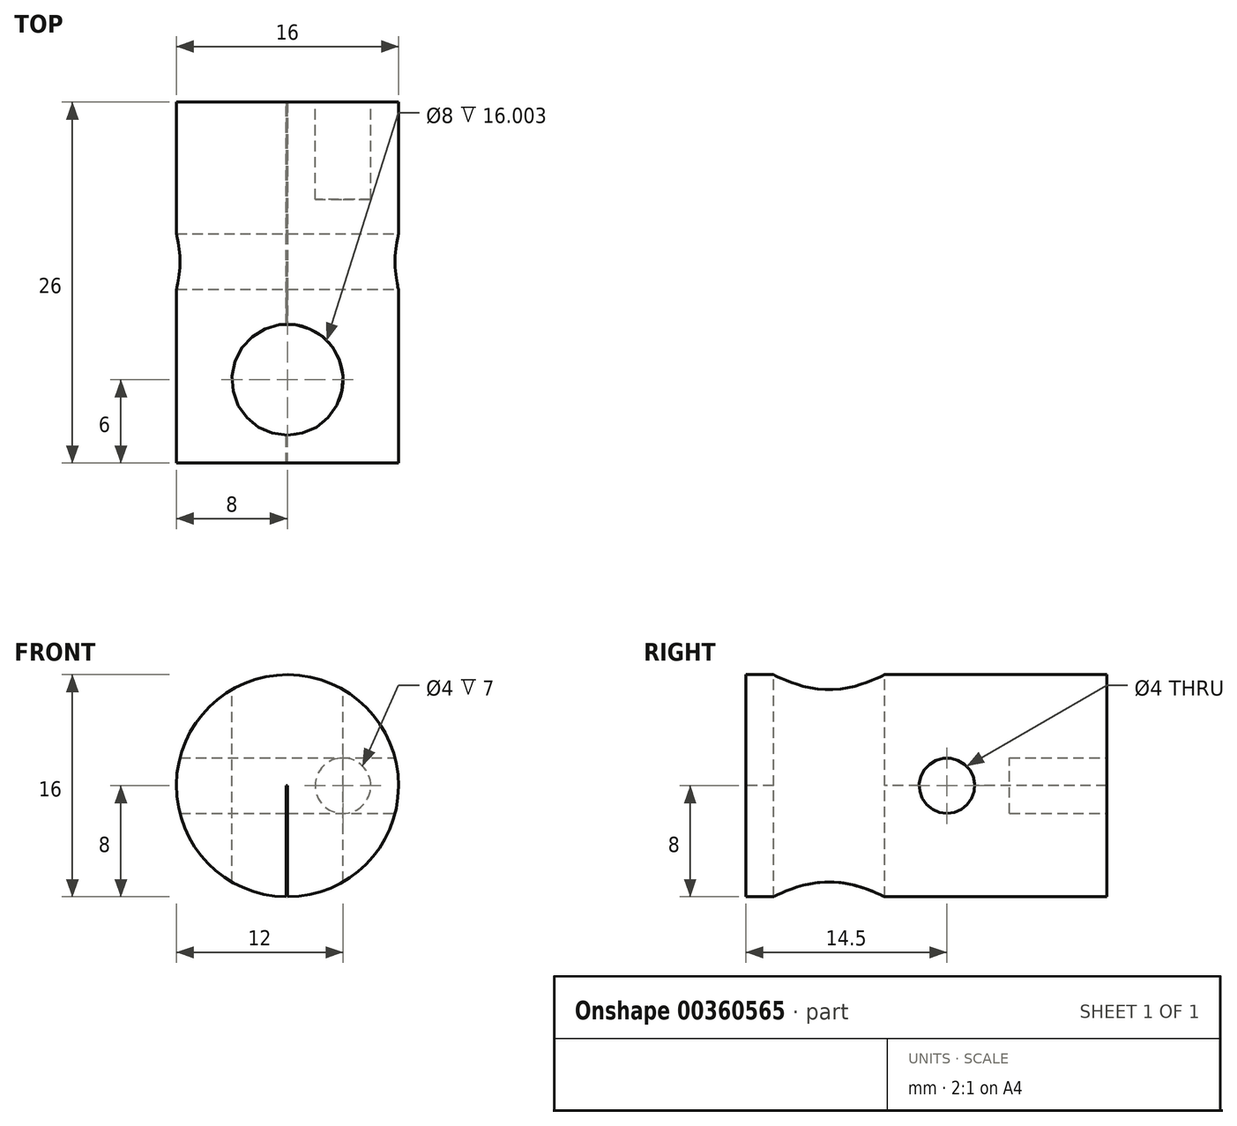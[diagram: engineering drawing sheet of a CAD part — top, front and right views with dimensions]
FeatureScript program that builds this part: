
annotation { "Feature Type Name" : "Feature", "Feature Type Description" : "" }
export const myFeature = defineFeature(function(context is Context, id is Id, definition is map)
    precondition{}
    {
        {
            var Q0;
            Q0=qCreatedBy(makeId("Front.planeOp"),FACE);
            var sketch = newSketch(context, id + "F0", { "sketchPlane" : qUnion([Q0])});
            skCircle(sketch, "E0", {"center": v(0, 0) * mm, "radius": 8 * mm});
            skLineSegment(sketch, "E1", {"start": v(0, 0) * mm, "end": v(4, 0) * mm, "construction": true});
            skLineSegment(sketch, "E2", {"start": v(0, 0) * mm, "end": v(-3.93, 0) * mm, "construction": true});
            skCircle(sketch, "E3", {"center": v(4, 0) * mm, "radius": 2 * mm});
            skSolve(sketch);
        }
        {
            var Q0;
            Q0=makeQuery(id+"F0.imprint","IMPRINT",FACE,{"disambiguationData":[TD([[makeQuery(id+"F0.imprint","IMPRINT",EDGE,{"derivedFrom":sQuery(id+"F0.wireOp",EDGE,"E0")}),1.0]])]});
            var Q1;
            Q1=makeQuery(id+"F0.imprint","IMPRINT",FACE,{"disambiguationData":[TD([[makeQuery(id+"F0.imprint","IMPRINT",EDGE,{"derivedFrom":sQuery(id+"F0.wireOp",EDGE,"E3")}),1.0]])]});
            extrude(context, id + "F1", {"entities" : qUnion([Q0, Q1]), "depth" : 26 * mm});
        }
        {
            var Q0;
            Q0=qCreatedBy(makeId("Top.planeOp"),FACE);
            var sketch = newSketch(context, id + "F2", { "sketchPlane" : qUnion([Q0])});
            skLineSegment(sketch, "E4", {"start": v(0, 0) * mm, "end": v(0, -20) * mm, "construction": true});
            skCircle(sketch, "E5", {"center": v(0, -20) * mm, "radius": 4 * mm});
            skSolve(sketch);
        }
        {
            var Q0;
            Q0 = qSketchRegion(id + "F2", true);
            extrude(context, id + "F3", {"entities" : qUnion([Q0]), "operationType" : NewBodyOperationType.REMOVE, "oppositeDirection" : true, "depth" : 25 * mm, "hasSecondDirection" : true, "secondDirectionOppositeDirection" : false, "secondDirectionDepth" : 25 * mm});
        }
        {
            var Q0;
            Q0=makeQuery(id+"F0.imprint","IMPRINT",FACE,{"disambiguationData":[TD([[makeQuery(id+"F0.imprint","IMPRINT",EDGE,{"derivedFrom":sQuery(id+"F0.wireOp",EDGE,"E3")}),1.0]])]});
            extrude(context, id + "F4", {"entities" : qUnion([Q0]), "operationType" : NewBodyOperationType.REMOVE, "depth" : 7 * mm});
        }
        {
            var Q0;
            Q0=qCreatedBy(makeId("Right.planeOp"),FACE);
            var sketch = newSketch(context, id + "F5", { "sketchPlane" : qUnion([Q0])});
            skLineSegment(sketch, "E6", {"start": v(0, 0) * mm, "end": v(-11.5, 0) * mm, "construction": true});
            skCircle(sketch, "E7", {"center": v(-11.5, 0) * mm, "radius": 2 * mm});
            skSolve(sketch);
        }
        {
            var Q0;
            Q0 = qSketchRegion(id + "F5", true);
            extrude(context, id + "F6", {"entities" : qUnion([Q0]), "operationType" : NewBodyOperationType.REMOVE, "oppositeDirection" : true, "depth" : 25 * mm, "hasSecondDirection" : true, "secondDirectionOppositeDirection" : false, "secondDirectionDepth" : 25 * mm});
        }
        {
            var Q0;
            Q0=qCreatedBy(makeId("Top.planeOp"),FACE);
            var sketch = newSketch(context, id + "F7", { "sketchPlane" : qUnion([Q0])});
            skLineSegment(sketch, "E8.bottom", {"start": v(0, 0) * mm, "end": v(-0.1, 0) * mm});
            skLineSegment(sketch, "E8.top", {"start": v(0, -30) * mm, "end": v(-0.1, -30) * mm});
            skLineSegment(sketch, "E8.left", {"start": v(0, 0) * mm, "end": v(0, -30) * mm});
            skLineSegment(sketch, "E8.right", {"start": v(-0.1, 0) * mm, "end": v(-0.1, -30) * mm});
            skSolve(sketch);
        }
        {
            var Q0;
            Q0 = qSketchRegion(id + "F7", true);
            extrude(context, id + "F8", {"entities" : qUnion([Q0]), "operationType" : NewBodyOperationType.REMOVE, "oppositeDirection" : true, "depth" : 25 * mm});
        }
    });
